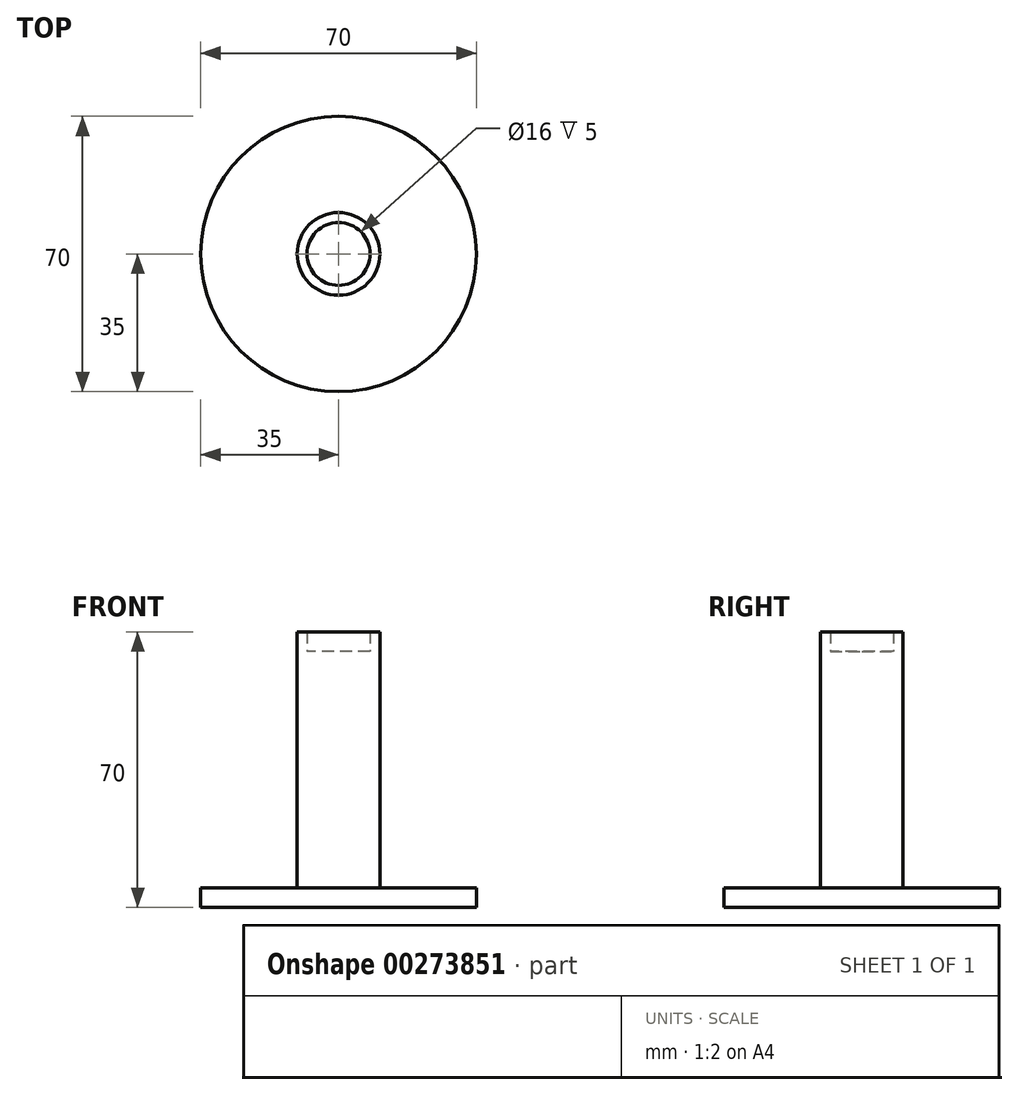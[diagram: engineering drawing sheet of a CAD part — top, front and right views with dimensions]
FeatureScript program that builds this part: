
annotation { "Feature Type Name" : "Feature", "Feature Type Description" : "" }
export const myFeature = defineFeature(function(context is Context, id is Id, definition is map)
    precondition{}
    {
        {
            var Q0;
            Q0=qCreatedBy(makeId("Top.planeOp"),FACE);
            var sketch = newSketch(context, id + "F0", { "sketchPlane" : qUnion([Q0])});
            skCircle(sketch, "E0", {"center": v(0, 0) * mm, "radius": 25 * mm, "construction": true});
            skCircle(sketch, "E1", {"center": v(0, 0) * mm, "radius": 10.5 * mm});
            skCircle(sketch, "E2", {"center": v(0, 0) * mm, "radius": 8 * mm});
            skCircle(sketch, "E3", {"center": v(0, 0) * mm, "radius": 35 * mm});
            skSolve(sketch);
        }
        {
            var Q0;
            Q0=makeQuery(id+"F0.imprint","IMPRINT",FACE,{"disambiguationData":[TD([[makeQuery(id+"F0.imprint","IMPRINT",EDGE,{"derivedFrom":sQuery(id+"F0.wireOp",EDGE,"E1")}),-1.0]])]});
            extrude(context, id + "F1", {"entities" : qUnion([Q0]), "depth" : 5 * mm});
        }
        {
            var Q0;
            Q0=makeQuery(id+"F0.imprint","IMPRINT",FACE,{"disambiguationData":[TD([[makeQuery(id+"F0.imprint","IMPRINT",EDGE,{"derivedFrom":sQuery(id+"F0.wireOp",EDGE,"E1")}),1.0]])]});
            extrude(context, id + "F2", {"entities" : qUnion([Q0]), "operationType" : NewBodyOperationType.ADD, "depth" : 70 * mm});
        }
        {
            var Q0;
            Q0=makeQuery(id+"F0.imprint","IMPRINT",FACE,{"disambiguationData":[TD([[makeQuery(id+"F0.imprint","IMPRINT",EDGE,{"derivedFrom":sQuery(id+"F0.wireOp",EDGE,"E2")}),1.0]])]});
            extrude(context, id + "F3", {"entities" : qUnion([Q0]), "operationType" : NewBodyOperationType.ADD, "depth" : 65 * mm});
        }
    });
